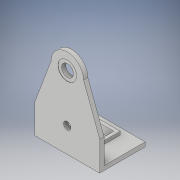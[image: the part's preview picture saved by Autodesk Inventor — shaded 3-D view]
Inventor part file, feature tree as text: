
AUTODESK INVENTOR PART (.ipt)
format: ipt  version: 2019 (Build 230136000, 136)  size: 326,144 bytes
history: native  units: mm
features: extrude x6, sketch x6, projected_geometry x1
ambient origin geometry x8: Origin, YZ Plane, XZ Plane, XY Plane, X Axis, Y Axis, Z Axis, Center Point
bodies: Body1 (feature_tree)
feature tree (13):
  extrude  "Extrusion1"  Depth=10.0mm
  extrude  "Extrusion2"  Depth=5.5mm
  extrude  "Extrusion3"  Depth=30.0mm
  extrude  "Extrusion4"  Depth=3.4mm
  extrude  "Extrusion5"  Depth=3.5mm TaperAngle=0.0deg
  extrude  "Extrusion6"  Depth=19.0mm TaperAngle=0.0deg
  sketch  "Sketch2"  dims[d15=30.0mm d16=10.0mm]
  sketch  "Sketch3"  dims[d17=15.0mm d18=5.5mm]
  projected_geometry  "Projected Loop1"
  sketch  "Sketch4"  dims[d19=30.0mm d20=8.0mm]
  sketch  "Sketch5"  dims[d21=15.0mm d22=3.4mm]
  sketch  "Sketch6"  dims[d23=2.0mm d24=0.0mm d25=3.5mm d26=0.0mm]
  sketch  "Sketch7"  dims[d27=2.0mm d28=19.0mm d29=0.0mm d31=10.0mm d32=9.5mm d33=10.0mm d34=10.0mm d35=0.0mm d36=1.5mm d37=1.5mm d38=0.0mm d39=8.55mm d40=0.1mm d41=0.0mm]
